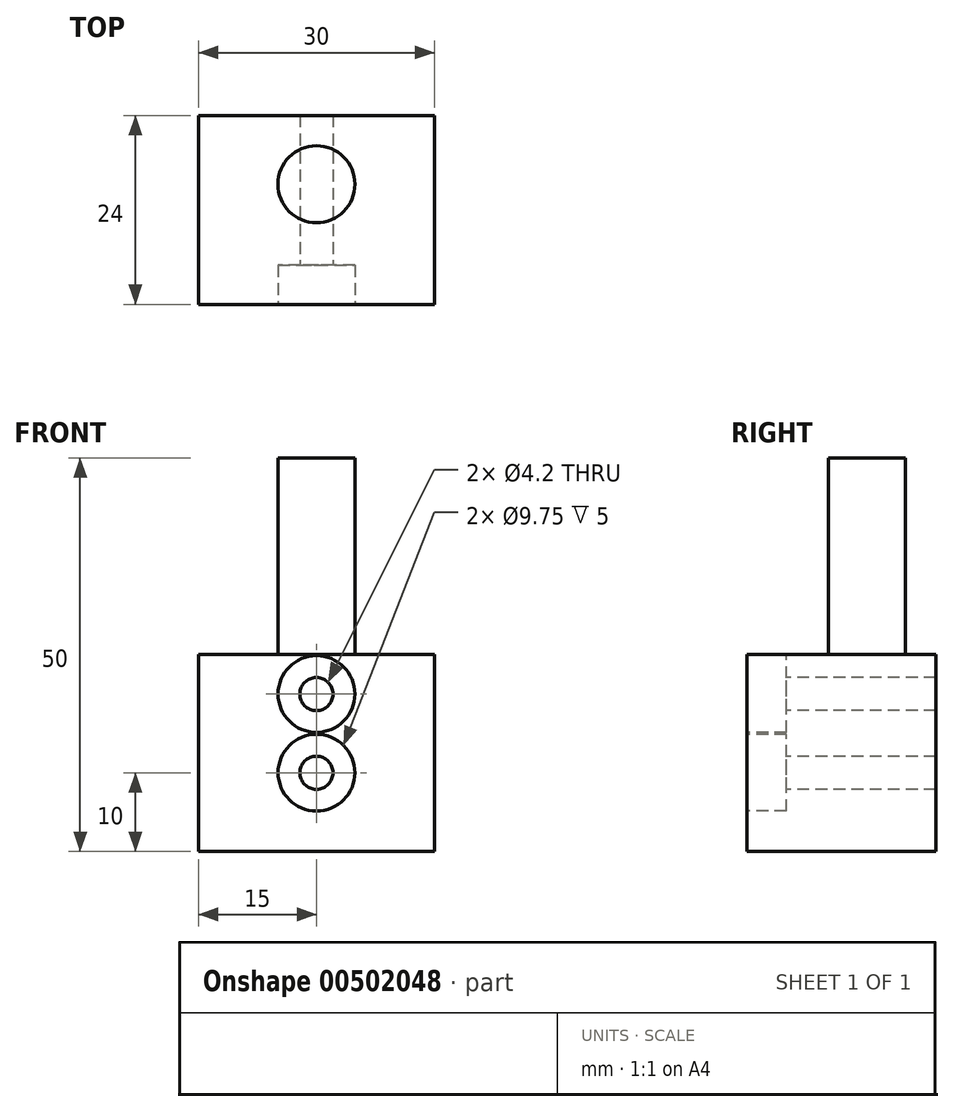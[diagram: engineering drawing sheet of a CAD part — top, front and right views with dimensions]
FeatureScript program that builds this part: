
annotation { "Feature Type Name" : "Feature", "Feature Type Description" : "" }
export const myFeature = defineFeature(function(context is Context, id is Id, definition is map)
    precondition{}
    {
        {
            var Q0;
            Q0=qCreatedBy(makeId("Top.planeOp"),FACE);
            var sketch = newSketch(context, id + "F0", { "sketchPlane" : qUnion([Q0])});
            skLineSegment(sketch, "E0.bottom", {"start": v(0, 0) * mm, "end": v(30, 0) * mm});
            skLineSegment(sketch, "E0.top", {"start": v(0, -24) * mm, "end": v(30, -24) * mm});
            skLineSegment(sketch, "E0.left", {"start": v(0, 0) * mm, "end": v(0, -24) * mm});
            skLineSegment(sketch, "E0.right", {"start": v(30, 0) * mm, "end": v(30, -24) * mm});
            skSolve(sketch);
        }
        {
            var Q0;
            Q0 = qSketchRegion(id + "F0", true);
            extrude(context, id + "F1", {"entities" : qUnion([Q0]), "depth" : 25 * mm});
        }
        {
            var Q0;
            Q0=makeQuery(id+"F1.opExtrude","SWEPT_FACE",FACE,{"disambiguationData":[OSD([sQuery(id+"F0.wireOp",EDGE,"E0.top")])]});
            var sketch = newSketch(context, id + "F2", { "sketchPlane" : qUnion([Q0])});
            skLineSegment(sketch, "E1", {"start": v(15, 0) * mm, "end": v(15, 10) * mm});
            skLineSegment(sketch, "E2", {"start": v(15, 10) * mm, "end": v(15, 20) * mm});
            skSolve(sketch);
        }
        {
            var Q0;
            Q0=sQuery(id+"F2.wireOp",VERTEX,"E2.end");
            var Q1;
            Q1=sQuery(id+"F2.wireOp",VERTEX,"E2.start");
            var Q2;
            Q2=makeQuery(id+"F1.opExtrude","SWEPT_BODY",BODY,{"disambiguationData":[OSD([sQuery(id+"F0.wireOp",EDGE,"E0.bottom"),sQuery(id+"F0.wireOp",EDGE,"E0.top"),sQuery(id+"F0.wireOp",EDGE,"E0.left"),sQuery(id+"F0.wireOp",EDGE,"E0.right")])]});
            hole(context, id + "F3", {"style" : HoleStyle.C_BORE, "endStyle" : HoleEndStyle.THROUGH, "standardTappedOrClearance" : lookupTablePath({ "standard" : "ISO", "engagement" : "75%", "pitch" : "0.8 mm", "size" : "M5", "type" : "Tapped" }), "standardBlindInLast" : lookupTablePath({ "standard" : "ISO", "fit" : "Normal", "engagement" : "75%", "pitch" : "0.8 mm", "size" : "M5", "type" : "Clearance & tapped" }), "holeDiameter" : 4.2 * mm, "cBoreDiameter" : 9.75 * mm, "cBoreDepth" : 5 * mm, "majorDiameter" : 5 * mm, "showTappedDepth" : true, "isTappedThrough" : true, "tappedDepth" : 12 * mm, "tapClearance" : 3, "locations" : qUnion([Q0, Q1]), "scope" : qUnion([Q2])});
        }
        {
            var Q0;
            Q0=makeQuery(id+"F1.opExtrude","CAP_FACE",FACE,{"disambiguationData":[OSD([sQuery(id+"F0.wireOp",EDGE,"E0.bottom"),sQuery(id+"F0.wireOp",EDGE,"E0.top"),sQuery(id+"F0.wireOp",EDGE,"E0.left"),sQuery(id+"F0.wireOp",EDGE,"E0.right")])],"isStart":false});
            var sketch = newSketch(context, id + "F4", { "sketchPlane" : qUnion([Q0])});
            skCircle(sketch, "E3", {"center": v(15, -8.74) * mm, "radius": 4.89 * mm});
            skPoint(sketch, "E3.centerSnap0", {"position": v(15, 0) * mm});
            skSolve(sketch);
        }
        {
            var Q0;
            Q0 = qSketchRegion(id + "F4", true);
            extrude(context, id + "F5", {"entities" : qUnion([Q0]), "operationType" : NewBodyOperationType.ADD, "depth" : 25 * mm, "offsetDistance" : 25 * mm});
        }
    });
